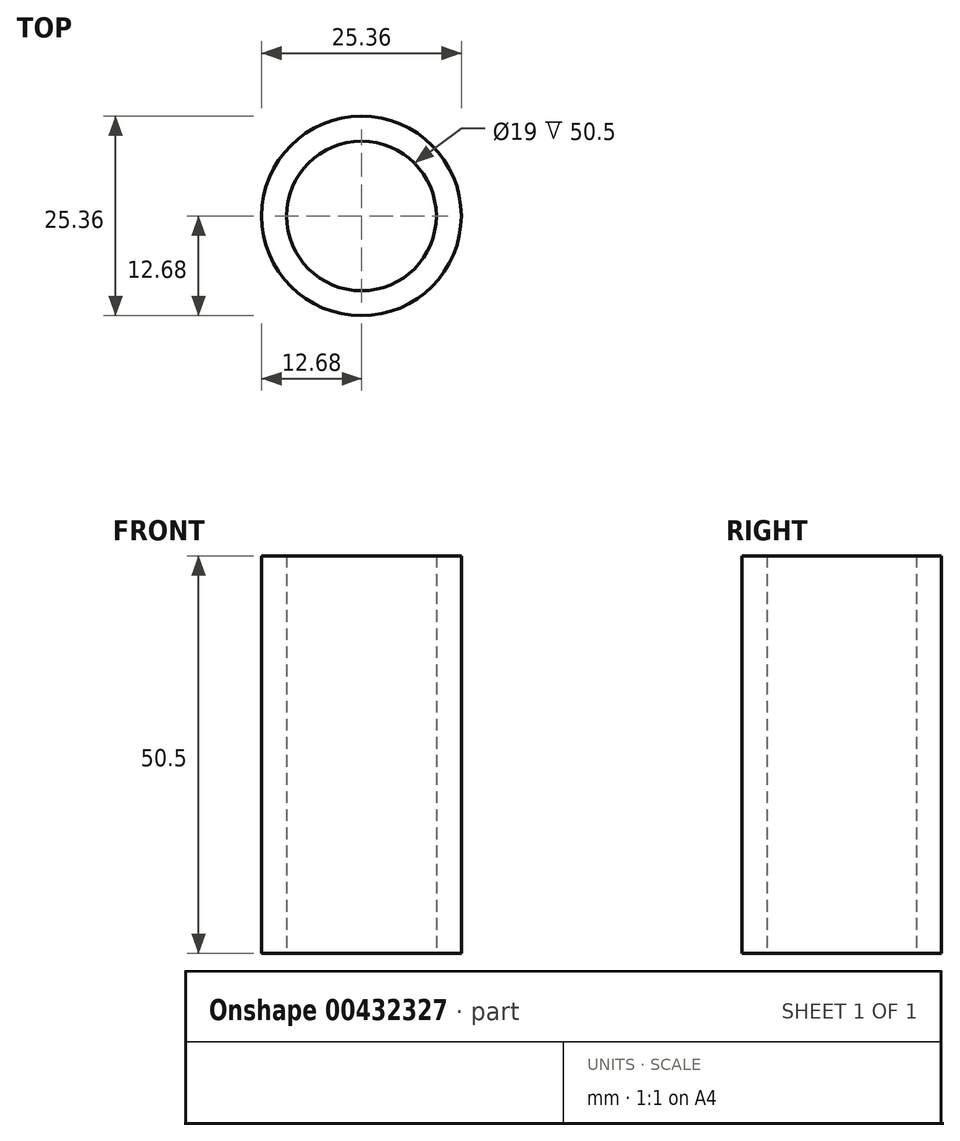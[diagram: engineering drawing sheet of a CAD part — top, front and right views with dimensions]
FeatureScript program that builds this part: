
annotation { "Feature Type Name" : "Feature", "Feature Type Description" : "" }
export const myFeature = defineFeature(function(context is Context, id is Id, definition is map)
    precondition{}
    {
        {
            var Q0;
            Q0=qCreatedBy(makeId("Top.planeOp"),FACE);
            var sketch = newSketch(context, id + "F0", { "sketchPlane" : qUnion([Q0])});
            skCircle(sketch, "E0", {"center": v(0, 0) * mm, "radius": 9.5 * mm});
            skCircle(sketch, "E1", {"center": v(0, 0) * mm, "radius": 12.68 * mm});
            skSolve(sketch);
        }
        {
            var Q0;
            Q0=makeQuery(id+"F0.imprint","IMPRINT",FACE,{"disambiguationData":[TD([[makeQuery(id+"F0.imprint","IMPRINT",EDGE,{"derivedFrom":sQuery(id+"F0.wireOp",EDGE,"E0")}),-1.0]])]});
            extrude(context, id + "F1", {"entities" : qUnion([Q0]), "depth" : 50.5 * mm});
        }
    });
